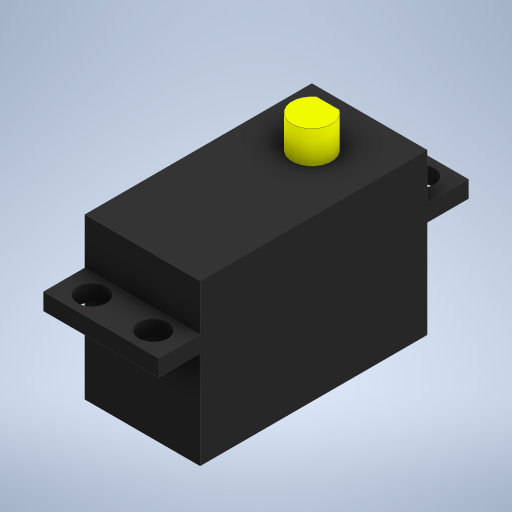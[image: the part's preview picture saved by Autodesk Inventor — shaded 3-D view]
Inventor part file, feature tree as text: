
AUTODESK INVENTOR PART (.ipt)
format: ipt  version: 2023.1 (Build 271208000, 208)  size: 258,048 bytes
history: native  units: mm
features: extrude x4, sketch x3, other x1
ambient origin geometry x8: Origin, YZ Plane, XZ Plane, XY Plane, X Axis, Y Axis, Z Axis, Center Point
bodies: Body1 (feature_tree)
feature tree (8):
  other  "솔리드1"
  sketch  "스케치1"
  extrude  "돌출1"  Depth=16.0mm
  extrude  "돌출2"  Depth=31.5mm
  extrude  "돌출3"  Depth=13.5mm TaperAngle=0.0deg
  extrude  "돌출4"  Depth=43.0mm
  sketch  "스케치2"
  sketch  "스케치4"
